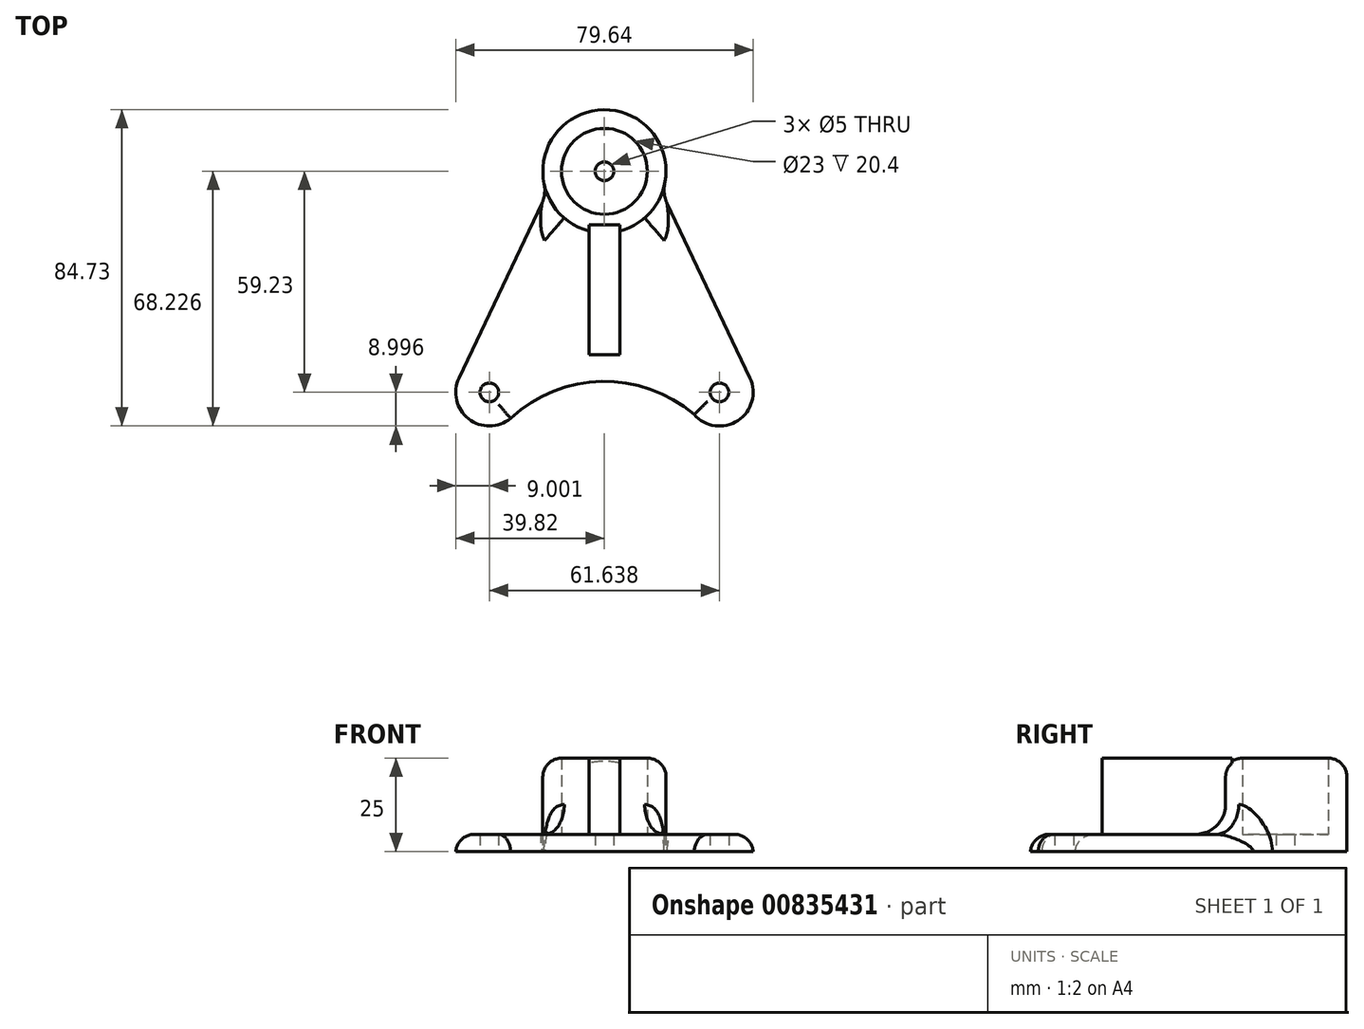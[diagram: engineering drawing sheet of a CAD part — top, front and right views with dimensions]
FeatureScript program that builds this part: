
annotation { "Feature Type Name" : "Feature", "Feature Type Description" : "" }
export const myFeature = defineFeature(function(context is Context, id is Id, definition is map)
    precondition{}
    {
        {
            var Q0;
            Q0=qCreatedBy(makeId("Top.planeOp"),FACE);
            var sketch = newSketch(context, id + "F0", { "sketchPlane" : qUnion([Q0])});
            skCircle(sketch, "E0", {"center": v(0, 21.49) * mm, "radius": 11.5 * mm});
            skCircle(sketch, "E1", {"center": v(0, 21.49) * mm, "radius": 2.5 * mm});
            skLineSegment(sketch, "E2", {"start": v(-10.4, 26.4) * mm, "end": v(-40.32, -36.77) * mm});
            skCircle(sketch, "E3", {"center": v(-30.82, -37.74) * mm, "radius": 9 * mm});
            skCircle(sketch, "E4.MirrorC", {"center": v(30.82, -37.74) * mm, "radius": 9 * mm});
            skLineSegment(sketch, "E5.MirrorCS", {"start": v(10.4, 26.4) * mm, "end": v(40.32, -36.77) * mm, "construction": true});
            skLineSegment(sketch, "E6.MirrorCS", {"start": v(10.4, 26.4) * mm, "end": v(40.32, -36.77) * mm});
            skCircle(sketch, "E7", {"center": v(-30.82, -37.74) * mm, "radius": 2.5 * mm});
            skCircle(sketch, "E8", {"center": v(30.82, -37.74) * mm, "radius": 2.5 * mm});
            skArc(sketch, "E9", {"start": v(24.06, -43.69) * mm, "mid": v(-0.73, -34.8) * mm, "end": v(-25.12, -44.71) * mm});
            skCircle(sketch, "E10", {"center": v(0, 21.49) * mm, "radius": 16.5 * mm});
            skSolve(sketch);
        }
        {
            var Q0;
            {var subQ0=sQuery(id+"F0.wireOp",EDGE,"E2");var subQ1=sQuery(id+"F0.wireOp",EDGE,"E0");var subQ2=makeQuery(id+"F0.imprint","INTERSECT",VERTEX,{"derivedFrom":[subQ1,subQ0]});Q0=makeQuery(id+"F0.imprint","IMPRINT",FACE,{"disambiguationData":[TD([[makeQuery(id+"F0.imprint","IMPRINT",EDGE,{"disambiguationData":[TD([[subQ2,1.0]])],"derivedFrom":subQ1}),-1.0]])]});}
            var Q1;
            {var subQ0=sQuery(id+"F0.wireOp",EDGE,"E2");var subQ1=sQuery(id+"F0.wireOp",EDGE,"E0");var subQ2=makeQuery(id+"F0.imprint","INTERSECT",VERTEX,{"derivedFrom":[subQ1,subQ0]});Q1=makeQuery(id+"F0.imprint","IMPRINT",FACE,{"disambiguationData":[TD([[makeQuery(id+"F0.imprint","IMPRINT",EDGE,{"disambiguationData":[TD([[subQ2,-1.0]])],"derivedFrom":subQ1}),-1.0]])]});}
            var Q2;
            {var subQ5=sQuery(id+"F0.wireOp",EDGE,"E3");var subQ6=sQuery(id+"F0.wireOp",EDGE,"E2");var subQ7=makeQuery(id+"F0.imprint","INTERSECT",VERTEX,{"derivedFrom":[subQ6,subQ5]});Q2=makeQuery(id+"F0.imprint","IMPRINT",FACE,{"disambiguationData":[TD([[makeQuery(id+"F0.imprint","IMPRINT",EDGE,{"disambiguationData":[TD([[subQ7,1.0]])],"derivedFrom":subQ6}),1.0]])]});}
            var Q3;
            Q3=makeQuery(id+"F0.imprint","IMPRINT",FACE,{"disambiguationData":[TD([[makeQuery(id+"F0.imprint","IMPRINT",EDGE,{"derivedFrom":sQuery(id+"F0.wireOp",EDGE,"E8")}),-1.0]])]});
            var Q4;
            Q4=makeQuery(id+"F0.imprint","IMPRINT",FACE,{"disambiguationData":[TD([[makeQuery(id+"F0.imprint","IMPRINT",EDGE,{"derivedFrom":sQuery(id+"F0.wireOp",EDGE,"E7")}),-1.0]])]});
            var Q5;
            Q5=makeQuery(id+"F0.imprint","IMPRINT",FACE,{"disambiguationData":[TD([[makeQuery(id+"F0.imprint","IMPRINT",EDGE,{"derivedFrom":sQuery(id+"F0.wireOp",EDGE,"E1")}),-1.0]])]});
            extrude(context, id + "F1", {"entities" : qUnion([Q0, Q1, Q2, Q3, Q4, Q5]), "depth" : 4.6 * mm, "offsetDistance" : 25 * mm});
        }
        {
            var Q0;
            {var subQ0=sQuery(id+"F0.wireOp",EDGE,"E2");var subQ1=sQuery(id+"F0.wireOp",EDGE,"E0");var subQ2=makeQuery(id+"F0.imprint","INTERSECT",VERTEX,{"derivedFrom":[subQ1,subQ0]});Q0=makeQuery(id+"F0.imprint","IMPRINT",FACE,{"disambiguationData":[TD([[makeQuery(id+"F0.imprint","IMPRINT",EDGE,{"disambiguationData":[TD([[subQ2,1.0]])],"derivedFrom":subQ1}),-1.0]])]});}
            var Q1;
            {var subQ0=sQuery(id+"F0.wireOp",EDGE,"E2");var subQ1=sQuery(id+"F0.wireOp",EDGE,"E0");var subQ2=makeQuery(id+"F0.imprint","INTERSECT",VERTEX,{"derivedFrom":[subQ1,subQ0]});Q1=makeQuery(id+"F0.imprint","IMPRINT",FACE,{"disambiguationData":[TD([[makeQuery(id+"F0.imprint","IMPRINT",EDGE,{"disambiguationData":[TD([[subQ2,-1.0]])],"derivedFrom":subQ1}),-1.0]])]});}
            extrude(context, id + "F2", {"entities" : qUnion([Q0, Q1]), "operationType" : NewBodyOperationType.ADD, "depth" : 25 * mm, "offsetDistance" : 25 * mm});
        }
        {
            var Q0;
            Q0=makeQuery(id+"F2.opExtrude","CAP_EDGE",EDGE,{"disambiguationData":[OSD([sQuery(id+"F0.wireOp",EDGE,"E10")])],"isStart":false});
            var Q1;
            Q1=makeQuery(id+"F1.opExtrude","CAP_EDGE",EDGE,{"disambiguationData":[OSD([sQuery(id+"F0.wireOp",EDGE,"E2")])],"isStart":false});
            var Q2;
            Q2=makeQuery(id+"F1.opExtrude","CAP_EDGE",EDGE,{"disambiguationData":[OSD([sQuery(id+"F0.wireOp",EDGE,"E9")])],"isStart":false});
            var Q3;
            Q3=makeQuery(id+"F1.opExtrude","CAP_EDGE",EDGE,{"disambiguationData":[OSD([sQuery(id+"F0.wireOp",EDGE,"E4.MirrorC")])],"isStart":false});
            fillet(context, id + "F3", {"entities" : qUnion([Q0, Q1, Q2, Q3]), "radius" : 5 * mm, "tangentPropagation" : true, "allowEdgeOverflow" : false});
        }
        {
            var Q0;
            {var subQ0=sQuery(id+"F0.wireOp",EDGE,"E10");Q0=makeQuery(id+"F2.boolean.opBoolean","INTERSECT",EDGE,{"derivedFrom":[makeQuery(id+"F1.opExtrude","CAP_FACE",FACE,{"disambiguationData":[OSD([sQuery(id+"F0.wireOp",EDGE,"E1"),sQuery(id+"F0.wireOp",EDGE,"E2"),sQuery(id+"F0.wireOp",EDGE,"E3"),sQuery(id+"F0.wireOp",EDGE,"E4.MirrorC"),sQuery(id+"F0.wireOp",EDGE,"E6.MirrorCS"),sQuery(id+"F0.wireOp",EDGE,"E7"),sQuery(id+"F0.wireOp",EDGE,"E8"),sQuery(id+"F0.wireOp",EDGE,"E9"),subQ0])],"isStart":false}),makeQuery(id+"F2.opExtrude","SWEPT_FACE",FACE,{"disambiguationData":[OSD([subQ0])]})]});}
            fillet(context, id + "F4", {"entities" : qUnion([Q0]), "radius" : 8 * mm, "tangentPropagation" : true, "allowEdgeOverflow" : false});
        }
        {
            var Q0;
            Q0=qCreatedBy(makeId("Top.planeOp"),FACE);
            var sketch = newSketch(context, id + "F5", { "sketchPlane" : qUnion([Q0])});
            skLineSegment(sketch, "E11.bottom", {"start": v(132.08, 62.57) * mm, "end": v(-132.08, 62.57) * mm});
            skLineSegment(sketch, "E11.top", {"start": v(132.08, -62.57) * mm, "end": v(-132.08, -62.57) * mm});
            skLineSegment(sketch, "E11.left", {"start": v(132.08, 62.57) * mm, "end": v(132.08, -62.57) * mm});
            skLineSegment(sketch, "E11.right", {"start": v(-132.08, 62.57) * mm, "end": v(-132.08, -62.57) * mm});
            skPoint(sketch, "E11.middle", {"position": v(0, 0) * mm});
            skLineSegment(sketch, "E12.bottom", {"start": v(-4.07, 7.15) * mm, "end": v(4.07, 7.15) * mm});
            skLineSegment(sketch, "E12.top", {"start": v(-4.07, -27.63) * mm, "end": v(4.07, -27.63) * mm});
            skLineSegment(sketch, "E12.left", {"start": v(-4.07, 7.15) * mm, "end": v(-4.07, -27.63) * mm});
            skLineSegment(sketch, "E12.right", {"start": v(4.07, 7.15) * mm, "end": v(4.07, -27.63) * mm});
            skPoint(sketch, "E12.middle", {"position": v(0, -10.24) * mm});
            skSolve(sketch);
        }
        {
            var Q0;
            Q0=makeQuery(id+"F5.imprint","IMPRINT",FACE,{"disambiguationData":[TD([[makeQuery(id+"F5.imprint","IMPRINT",EDGE,{"derivedFrom":sQuery(id+"F5.wireOp",EDGE,"E12.bottom")}),-1.0]])]});
            extrude(context, id + "F6", {"entities" : qUnion([Q0]), "operationType" : NewBodyOperationType.ADD, "depth" : 25 * mm, "offsetDistance" : 25 * mm});
        }
    });
